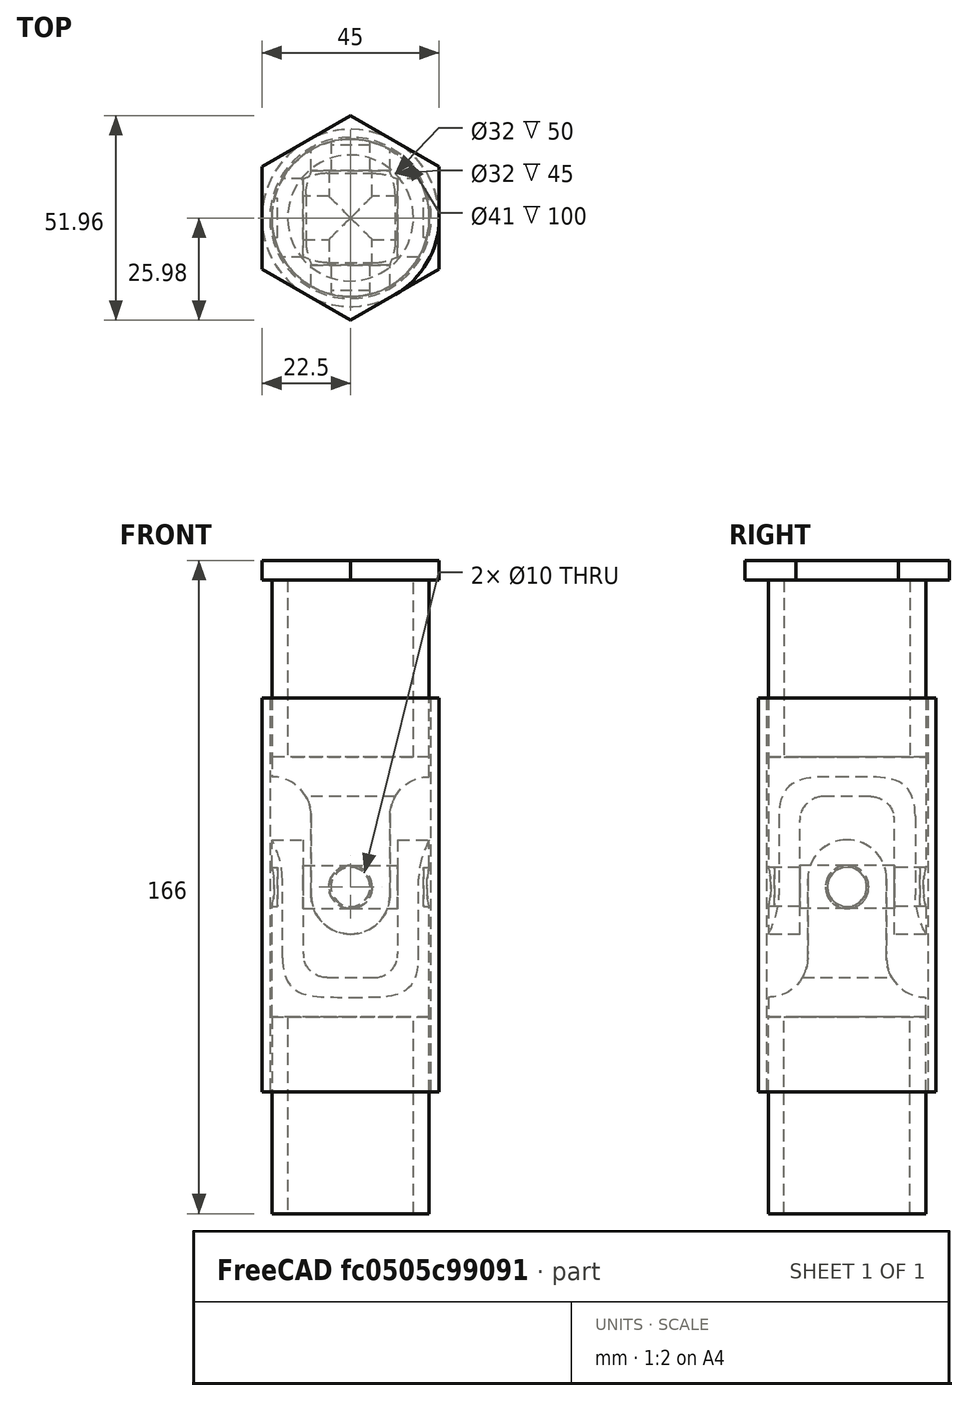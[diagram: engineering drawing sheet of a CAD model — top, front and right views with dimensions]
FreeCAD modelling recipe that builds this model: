
FCSTD DOCUMENT  (FreeCAD 0.21R33694 (Git))
Label: U_joint
License: All rights reserved
LicenseURL: http://en.wikipedia.org/wiki/All_rights_reserved
objects: Sketcher::SketchObject×7, Part::FeaturePython×5, Part::Extrusion×4, PartDesign::Pocket×3, PartDesign::Mirrored×2, Part::MultiFuse×2, Fem::ConstraintForce×2, PartDesign::AdditiveCylinder×1, PartDesign::Body×1, Part::Part2DObjectPython×1, Part::Compound×1, App::MaterialObjectPython×1, Fem::ConstraintFixed×1, Fem::FeaturePython×1, Fem::FemMeshObjectPython×1, Fem::FemSolverObjectPython×1, Fem::FemAnalysis×1
note: 31 computed .brp shape members not serialized (recipe doc carries the construction recipe); baked Part::Feature solids carry a one-line shape summary decoded from their .brp

FEATURE [PartDesign::AdditiveCylinder] Cylinder
  Angle = 360
  AttacherType = Attacher::AttachEngine3D
  FirstAngle = 0
  Height = 45
  MapMode = 5
  Radius = 20
  Refine = true
  SecondAngle = 0
  Support = -> [XY_Plane]
FEATURE [Sketcher::SketchObject] Sketch
  FullyConstrained = true
  MapMode = 5
  Placement = pos=(0,0,0) rot=(1,0,0;1.5708rad)
  Support = -> [XZ_Plane]
  sketch-geometry (7):
    g0: LineSegment StartX=25 StartY=0 StartZ=0 EndX=0 EndY=0 EndZ=0
    g1: ArcOfCircle CenterX=1.85e-14 CenterY=10 CenterZ=0 NormalX=0 NormalY=0 NormalZ=1 AngleXU=0 Radius=10 StartAngle=3.14159 EndAngle=4.71239
    g2: LineSegment StartX=-10 StartY=10 StartZ=0 EndX=-10 EndY=30 EndZ=0
    g3: ArcOfCircle CenterX=-20 CenterY=30 CenterZ=0 NormalX=0 NormalY=0 NormalZ=1 AngleXU=0 Radius=10 StartAngle=0 EndAngle=1.5708
    g4: LineSegment StartX=-20 StartY=40 StartZ=0 EndX=-30 EndY=40 EndZ=0
    g5: LineSegment StartX=-30 StartY=40 StartZ=0 EndX=-30 EndY=0 EndZ=0
    g6: LineSegment StartX=-30 StartY=0 StartZ=0 EndX=0 EndY=0 EndZ=0
  constraints (18):
    c: PointOnObject(g0,g-1)
    c: Coincident(g0,g-1)
    c: Tangent(g0,g1) = 1.5708
    c: Tangent(g1,g2) = 1.5708
    c: Tangent(g2,g3) = -1.5708
    c: Tangent(g3,g4) = -1.5708
    c: Coincident(g4,g5)
    c: PointOnObject(g5,g-1)
    c: Vertical(g5)
    c: Coincident(g5,g6)
    c: Coincident(g6,g0)
    c: Horizontal(g4)
    c: Vertical(g2)
    c: Equal(g3,g1)
    c: DistanceX(g1,g1) = 10
    c: DistanceY(g5,g5) = 40
    c: DistanceX(g4,g4) = 10
    c: DistanceX(g0,g0) = 25
FEATURE [PartDesign::Pocket] Pocket
  BaseFeature = -> Cylinder
  Direction = (0,1,-2e-16)
  Length = 5
  Length2 = 5
  Midplane = true
  Profile = -> Sketch
  ReferenceAxis = -> Sketch [N_Axis]
  Refine = true
  Type = 1
FEATURE [PartDesign::Mirrored] Mirrored
  BaseFeature = -> Pocket
  MirrorPlane = -> Sketch [V_Axis]
  Originals = -> [Pocket]
  Refine = true
FEATURE [Sketcher::SketchObject] Sketch001
  FullyConstrained = true
  MapMode = 5
  Placement = pos=(0,0,0) rot=(0.57735,0.57735,0.57735;2.0944rad)
  Support = -> [YZ_Plane]
  sketch-geometry (5):
    g0: LineSegment StartX=-12 StartY=0 StartZ=0 EndX=-12 EndY=29 EndZ=0
    g1: ArcOfCircle CenterX=-6 CenterY=29 CenterZ=0 NormalX=0 NormalY=0 NormalZ=1 AngleXU=0 Radius=6 StartAngle=1.5708 EndAngle=3.14159
    g2: LineSegment StartX=-6 StartY=35 StartZ=0 EndX=0 EndY=35 EndZ=0
    g3: LineSegment StartX=0 StartY=35 StartZ=0 EndX=0 EndY=0 EndZ=0
    g4: LineSegment StartX=0 StartY=0 StartZ=0 EndX=-12 EndY=0 EndZ=0
  constraints (13):
    c: PointOnObject(g0,g-1)
    c: Vertical(g0)
    c: Tangent(g0,g1) = 1.5708
    c: Tangent(g1,g2) = 1.5708
    c: Coincident(g2,g3)
    c: Coincident(g3,g-1)
    c: Vertical(g3)
    c: Coincident(g3,g4)
    c: Coincident(g4,g0)
    c: Horizontal(g2)
    c: DistanceX(g0,g1) = 6
    c: DistanceY(g3,g3) = 35
    c: DistanceX(g4,g4) = 12
FEATURE [PartDesign::Pocket] Pocket001
  BaseFeature = -> Mirrored
  Direction = (-1,2e-16,-3e-16)
  Length = 5
  Length2 = 5
  Midplane = true
  Profile = -> Sketch001
  ReferenceAxis = -> Sketch001 [N_Axis]
  Refine = true
  Type = 1
FEATURE [PartDesign::Mirrored] Mirrored001
  BaseFeature = -> Pocket001
  MirrorPlane = -> Sketch001 [V_Axis]
  Originals = -> [Pocket001]
  Refine = true
FEATURE [Sketcher::SketchObject] Sketch002
  FullyConstrained = true
  MapMode = 5
  Placement = pos=(0,0,0) rot=(1,0,0;1.5708rad)
  Support = -> [XZ_Plane]
  sketch-geometry (1):
    g0: Circle CenterX=0 CenterY=12 CenterZ=0 NormalX=0 NormalY=0 NormalZ=1 AngleXU=0 Radius=5
  constraints (3):
    c: PointOnObject(g0,g-2)
    c: Diameter(g0) = 10
    c: DistanceY(g-1,g0) = 12
FEATURE [PartDesign::Pocket] Pocket002
  BaseFeature = -> Mirrored001
  Direction = (0,1,2e-16)
  Length = 5
  Length2 = 5
  Midplane = true
  Profile = -> Sketch002
  ReferenceAxis = -> Sketch002 [N_Axis]
  Refine = true
  Type = 1
FEATURE [PartDesign::Body] Body
  Group = -> [Cylinder,Sketch,Pocket,Mirrored,Sketch001,Pocket001,Mirrored001,Sketch002,Pocket002]
  Origin = -> Origin
  Tip = -> Pocket002
FEATURE [Part::Part2DObjectPython] Line  # Draft 2D object (typed FeaturePython)
  Area = 0
  ChamferSize = 0
  Closed = false
  End = (1.8e-15,12,12)
  FilletRadius = 0
  Length = 24
  MakeFace = true
  Placement = pos=(0,-12,12) rot=(0.298693,0.65848,0.690787;2.21874rad)
  Points = (2) [(0,0,0),(20.7882,2.20183,11.79)]
  Start = (0,-12,12)
  Subdivisions = 0
FEATURE [Part::FeaturePython] Clone001  label="Pocket003"  # Draft clone (typed FeaturePython)
  AttacherType = Attacher::AttachEngine3D
  Fuse = false
  Objects = -> [Pocket002]
  Placement = pos=(0,1e-15,24) rot=(0.707107,-0.707107,0;3.14159rad)
  Scale = (1,1,1)
FEATURE [Sketcher::SketchObject] Sketch004
  FullyConstrained = true
  MapMode = 5
  Placement = pos=(0,0,45) rot=(0,0,1;0rad)
  Support = -> [Pocket002]
  sketch-geometry (3):
    g0: Circle CenterX=0 CenterY=0 CenterZ=0 NormalX=0 NormalY=0 NormalZ=1 AngleXU=0 Radius=20
    g1: Circle CenterX=0 CenterY=0 CenterZ=0 NormalX=0 NormalY=0 NormalZ=1 AngleXU=0 Radius=16
    g2: LineSegment StartX=16 StartY=0 StartZ=0 EndX=20 EndY=0 EndZ=0
  constraints (8):
    c: Coincident(g0,g-1)
    c: Diameter(g0) = 40
    c: Coincident(g1,g0)
    c: PointOnObject(g2,g1)
    c: PointOnObject(g2,g0)
    c: PointOnObject(g2,g-1)
    c: Horizontal(g2)
    c: DistanceX(g2,g2) = 4
FEATURE [Part::Extrusion] Extrude001  label="tube"
  Base = -> Sketch004
  Dir = (0,0,1)
  DirMode = 2
  FaceMakerClass = Part::FaceMakerBullseye
  LengthFwd = 50
  LengthRev = 0
  Solid = true
  Symmetric = false
FEATURE [Part::FeaturePython] Clone002  label="tube001"  # Draft clone (typed FeaturePython)
  AttacherType = Attacher::AttachEngine3D
  Fuse = false
  Objects = -> [Extrude001]
  Placement = pos=(1e-15,0,24) rot=(0,1,0;3.14159rad)
  Scale = (1,1,1)
FEATURE [Sketcher::SketchObject] Sketch005
  FullyConstrained = true
  sketch-geometry (2):
    g0: Circle CenterX=0 CenterY=0 CenterZ=0 NormalX=0 NormalY=0 NormalZ=1 AngleXU=0 Radius=22.5
    g1: Circle CenterX=0 CenterY=0 CenterZ=0 NormalX=0 NormalY=0 NormalZ=1 AngleXU=0 Radius=20.5
  constraints (4):
    c: Coincident(g0,g-1)
    c: Coincident(g1,g0)
    c: Diameter(g1) = 41
    c: Diameter(g0) = 45
FEATURE [Part::Extrusion] Extrude002  label="sleeve"
  Base = -> Sketch005
  Dir = (0,0,1)
  DirMode = 2
  FaceMakerClass = Part::FaceMakerBullseye
  LengthFwd = 60
  LengthRev = 40
  Solid = true
  Symmetric = false
FEATURE [Sketcher::SketchObject] Sketch006
  FullyConstrained = true
  MapMode = 5
  Placement = pos=(0,0,95) rot=(0,0,1;0rad)
  Support = -> [Extrude001]
  sketch-geometry (7):
    g0: LineSegment StartX=22.5 StartY=12.9904 StartZ=0 EndX=3.126e-13 EndY=25.9808 EndZ=0
    g1: LineSegment StartX=3.126e-13 StartY=25.9808 StartZ=0 EndX=-22.5 EndY=12.9904 EndZ=0
    g2: LineSegment StartX=-22.5 StartY=12.9904 StartZ=0 EndX=-22.5 EndY=-12.9904 EndZ=0
    g3: LineSegment StartX=-22.5 StartY=-12.9904 StartZ=0 EndX=1.812e-13 EndY=-25.9808 EndZ=0
    g4: LineSegment StartX=1.812e-13 StartY=-25.9808 StartZ=0 EndX=22.5 EndY=-12.9904 EndZ=0
    g5: LineSegment StartX=22.5 StartY=-12.9904 StartZ=0 EndX=22.5 EndY=12.9904 EndZ=0
    g6: Circle CenterX=0 CenterY=0 CenterZ=0 NormalX=0 NormalY=0 NormalZ=1 AngleXU=0 Radius=25.9808
  constraints (16):
    c: Coincident(g0,g1)
    c: Coincident(g1,g2)
    c: Coincident(g2,g3)
    c: Coincident(g3,g4)
    c: Coincident(g4,g5)
    c: Coincident(g5,g0)
    c: Equal(g0, g1-g5) x5
    c: PointOnObject(g0,g6)
    c: PointOnObject(g1,g6)
    c: PointOnObject(g2,g6)
    c: PointOnObject(g3,g6)
    c: PointOnObject(g4,g6)
    c: PointOnObject(g5,g6)
    c: Coincident(g6,g-1)
    c: Vertical(g5)
    c: DistanceX(g1,g0) = 45
FEATURE [Part::Extrusion] Extrude003  label="load_plate"
  Base = -> Sketch006
  Dir = (0,0,-1)
  DirMode = 0
  FaceMakerClass = Part::FaceMakerBullseye
  LengthFwd = 5
  LengthRev = 0
  Solid = true
  Symmetric = false
FEATURE [Part::MultiFuse] Fusion
  Refine = true
  Shapes = -> [Extrude001,Extrude003]
FEATURE [Part::FeaturePython] Clone003  label="Pocket004"  # Draft clone (typed FeaturePython)
  AttacherType = Attacher::AttachEngine3D
  Fuse = false
  Objects = -> [Pocket002]
  Scale = (1,1,1)
FEATURE [Sketcher::SketchObject] Sketch003
  ExternalGeometry = -> [Clone003]
  FullyConstrained = true
  Placement = pos=(0,0,0) rot=(1,0,0;1.5708rad)
  sketch-geometry (1):
    g0: Circle CenterX=0 CenterY=12 CenterZ=0 NormalX=0 NormalY=0 NormalZ=1 AngleXU=0 Radius=5.5
  constraints (2):
    c: Coincident(g0,g-3)
    c: Diameter(g0) = 11
FEATURE [Part::Extrusion] Extrude  label="bolt"
  Base = -> Sketch003
  Dir = (0,5,0)
  DirMode = 0
  FaceMakerClass = Part::FaceMakerBullseye
  LengthFwd = 37
  LengthRev = 0
  Solid = true
  Symmetric = true
FEATURE [Part::FeaturePython] Clone  label="bolt001"  # Draft clone (typed FeaturePython)
  AttacherType = Attacher::AttachEngine3D
  Fuse = false
  Objects = -> [Extrude]
  Placement = pos=(0,0,0) rot=(0,0,1;1.5708rad)
  Scale = (1,1,1)
FEATURE [Part::MultiFuse] Fusion001
  Refine = true
  Shapes = -> [Clone,Extrude,Clone003,Clone001]
FEATURE [Part::FeaturePython] BooleanFragments  # WARN: FeaturePython — macro-defined, semantics opaque (R4)
  Mode = 2
  Objects = -> [Fusion001,Fusion,Clone002]
  Tolerance = 0
FEATURE [Part::Compound] Compound
  Links = -> [BooleanFragments]
FEATURE [App::MaterialObjectPython] MaterialSolid  label="S355"  # material (typed FeaturePython)
  Category = 0
  Material = AuthorAndLicense=(c) 2013 Juergen Riegel (CC-BY 3.0),CardName=CalculiX-Steel,Density=7900 kg/m^3,+8 more (map truncated)
FEATURE [Fem::ConstraintFixed] ConstraintFixed
  NormalDirection = (0,0,-1)
  References = -> [Compound]
  Scale = 5
FEATURE [Fem::ConstraintForce] ConstraintForce  label="torque1"
  Direction = -> Compound [Edge137]
  DirectionVector = (0,1,0)
  Force = 22000
  NormalDirection = (1,0,0)
  Points = (12) [(22.5,-12.9904,90),(22.5,-4.33013,90),(22.5,4.33013,90),(22.5,12.9904,90),(22.5,-12.9904,92.5),(22.5,-4.33013,92.5),(22.5,4.33013,92.5),+5 more]
  References = -> [Compound]
FEATURE [Fem::ConstraintForce] ConstraintForce001  label="torque2"
  Direction = -> Compound [Edge143]
  DirectionVector = (-1.83e-14,-1,0)
  Force = 22000
  NormalDirection = (-1,1.83e-14,0)
  Points = (12) [(-22.5,12.9904,90),(-22.5,4.33013,90),(-22.5,-4.33013,90),(-22.5,-12.9904,90),(-22.5,12.9904,92.5),(-22.5,4.33013,92.5),(-22.5,-4.33013,92.5),+5 more]
  References = -> [Compound]
FEATURE [Fem::FeaturePython] MeshRegion  # FEM object (typed FeaturePython)
  CharacteristicLength = 1.5
  References = -> [Compound]
FEATURE [Fem::FemMeshObjectPython] FEMMeshGmsh  # FEM object (typed FeaturePython)
  Algorithm2D = 0
  Algorithm3D = 0
  CharacteristicLengthMax = 2.9
  CharacteristicLengthMin = 0
  CoherenceMesh = true
  ElementDimension = 0
  ElementOrder = 1
  GeometryTolerance = 1e-06
  GroupsOfNodes = false
  HighOrderOptimize = 0
  MeshRegionList = -> [MeshRegion]
  MeshSizeFromCurvature = 12
  OptimizeNetgen = false
  OptimizeStd = true
  Part = -> Compound
  RecombinationAlgorithm = 0
  Recombine3DAll = false
  RecombineAll = false
  SecondOrderLinear = false
FEATURE [Fem::FemSolverObjectPython] SolverCcxTools  # FEM object (typed FeaturePython)
  AnalysisType = 0
  BeamShellResultOutput3D = true
  BucklingFactors = 1
  EigenmodeHighLimit = 1000000
  EigenmodeLowLimit = 0
  EigenmodesCount = 10
  GeometricalNonlinearity = 0
  IterationsControlParameterCutb = 0.25,0.5,0.75,0.85,,,1.5,
  IterationsControlParameterIter = 4,8,9,200,10,400,,200,,
  IterationsControlParameterTimeUse = false
  IterationsThermoMechMaximum = 2000
  IterationsUserDefinedIncrementations = false
  IterationsUserDefinedTimeStepLength = false
  MaterialNonlinearity = 0
  MatrixSolverType = 0
  SplitInputWriter = true
  ThermoMechSteadyState = true
  TimeEnd = 1
  TimeInitialStep = 0.01
FEATURE [Fem::FemAnalysis] Analysis
  Group = -> [MaterialSolid,ConstraintFixed,ConstraintForce,ConstraintForce001,FEMMeshGmsh,SolverCcxTools]
